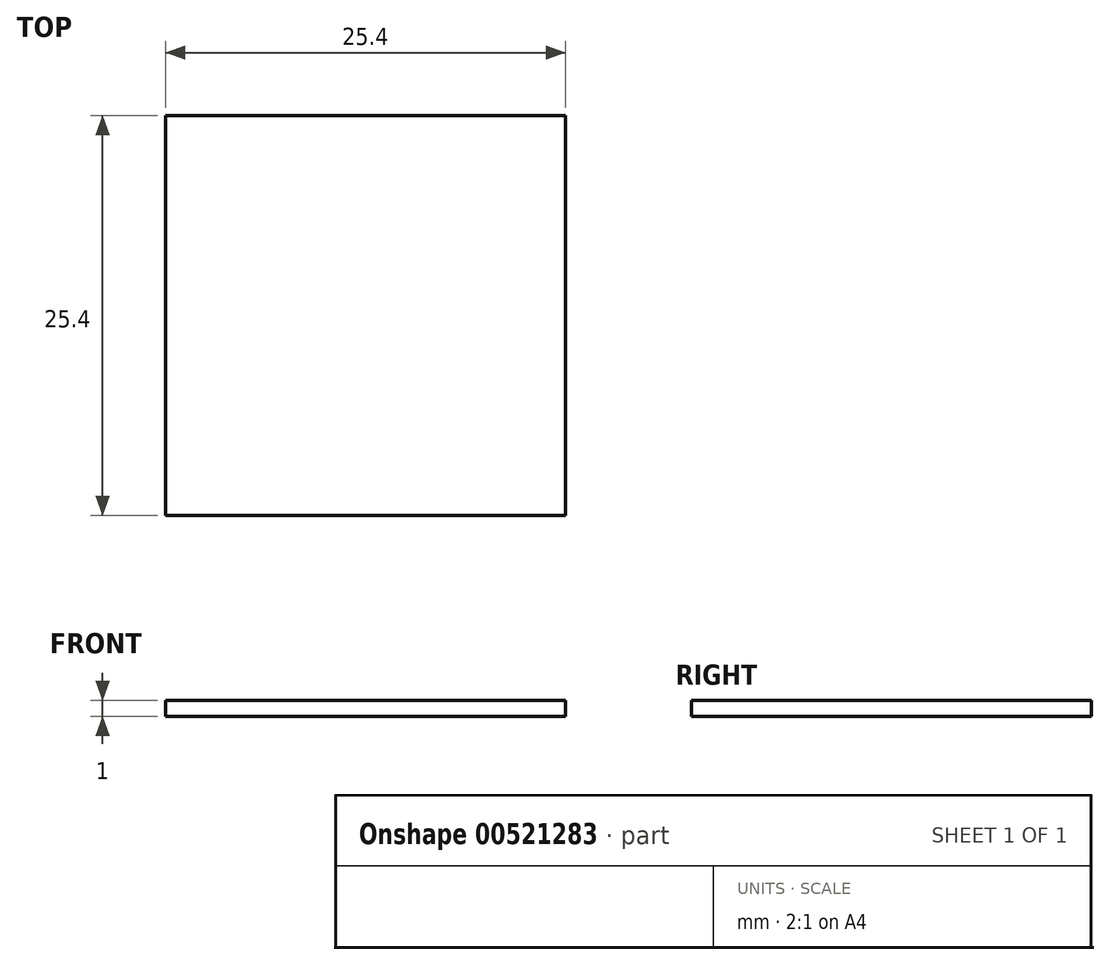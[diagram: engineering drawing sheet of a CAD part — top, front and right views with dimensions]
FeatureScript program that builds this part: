
annotation { "Feature Type Name" : "Feature", "Feature Type Description" : "" }
export const myFeature = defineFeature(function(context is Context, id is Id, definition is map)
    precondition{}
    {
        {
            var Q0;
            Q0=qCreatedBy(makeId("Top.planeOp"),FACE);
            var sketch = newSketch(context, id + "F0", { "sketchPlane" : qUnion([Q0])});
            skLineSegment(sketch, "E0.bottom", {"start": v(-12.7, 12.7) * mm, "end": v(12.7, 12.7) * mm});
            skLineSegment(sketch, "E0.top", {"start": v(-12.7, -12.7) * mm, "end": v(12.7, -12.7) * mm});
            skLineSegment(sketch, "E0.left", {"start": v(-12.7, 12.7) * mm, "end": v(-12.7, -12.7) * mm});
            skLineSegment(sketch, "E0.right", {"start": v(12.7, 12.7) * mm, "end": v(12.7, -12.7) * mm});
            skLineSegment(sketch, "E1", {"start": v(12.7, 12.7) * mm, "end": v(-12.7, -12.7) * mm});
            skSolve(sketch);
        }
        {
            var Q0;
            Q0 = qSketchRegion(id + "F0", true);
            extrude(context, id + "F1", {"entities" : qUnion([Q0]), "depth" : 1 * mm, "offsetDistance" : 25 * mm});
        }
    });
